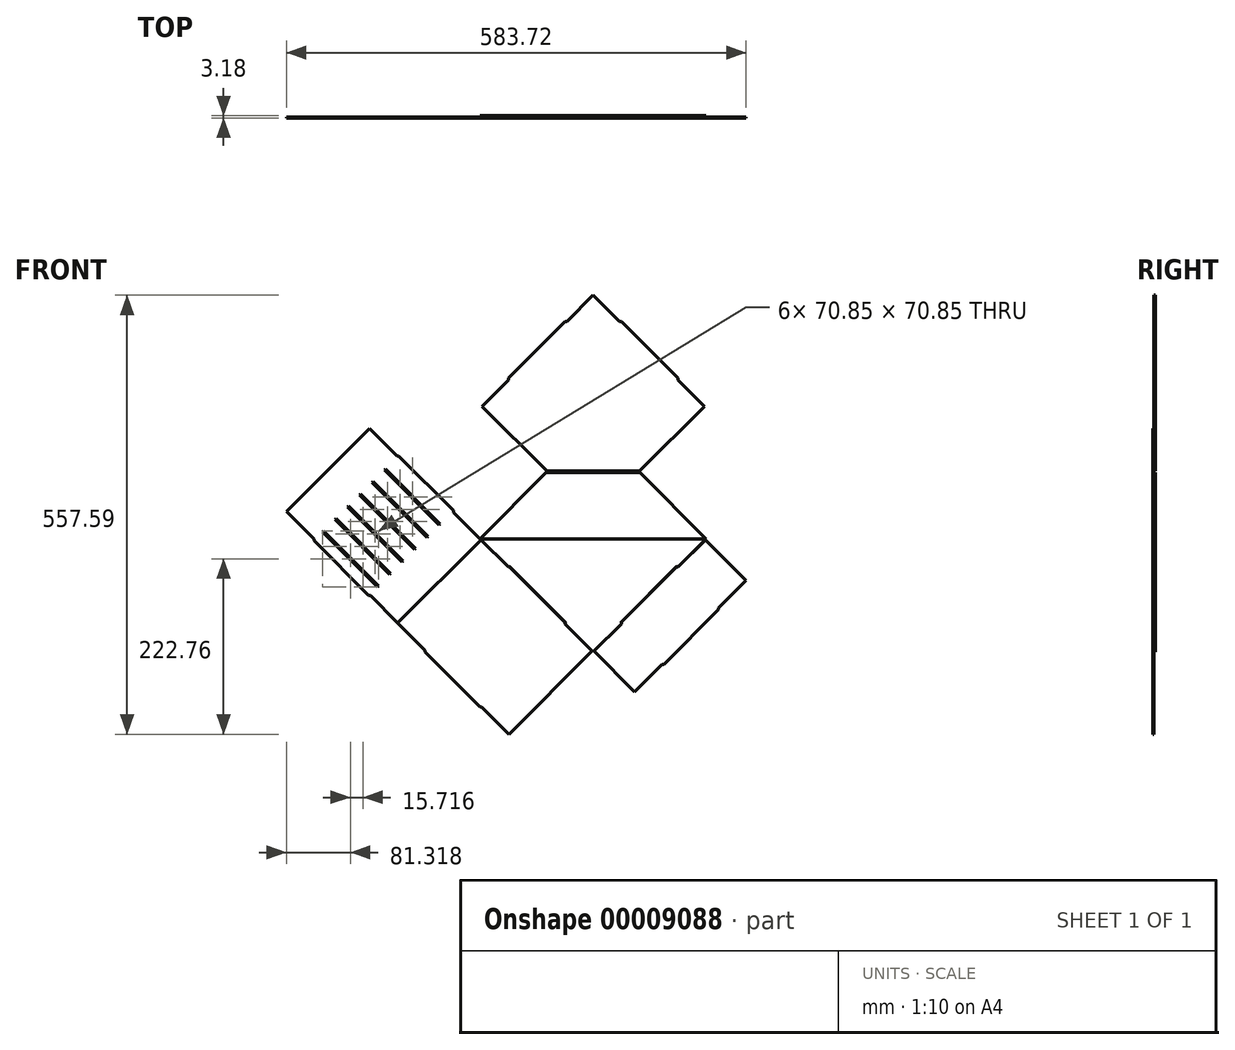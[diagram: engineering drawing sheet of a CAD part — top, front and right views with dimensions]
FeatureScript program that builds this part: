
annotation { "Feature Type Name" : "Feature", "Feature Type Description" : "" }
export const myFeature = defineFeature(function(context is Context, id is Id, definition is map)
    precondition{}
    {
        {
            var Q0;
            Q0=qCreatedBy(makeId("Front.planeOp"),FACE);
            var sketch = newSketch(context, id + "F0", { "sketchPlane" : qUnion([Q0])});
            skLineSegment(sketch, "E0", {"start": v(0, 0) * mm, "end": v(-143.68, 143.68) * mm});
            skLineSegment(sketch, "E1", {"start": v(-143.68, 143.68) * mm, "end": v(-59.52, 227.85) * mm});
            skLineSegment(sketch, "E2", {"start": v(59.52, 227.85) * mm, "end": v(143.68, 143.68) * mm});
            skLineSegment(sketch, "E3", {"start": v(143.68, 143.68) * mm, "end": v(0, 0) * mm});
            skLineSegment(sketch, "E4", {"start": v(-143.68, 143.68) * mm, "end": v(143.68, 143.68) * mm});
            skLineSegment(sketch, "E5", {"start": v(-35.92, 35.92) * mm, "end": v(-34.8, 37.04) * mm});
            skLineSegment(sketch, "E6", {"start": v(-34.8, 37.04) * mm, "end": v(-106.64, 108.89) * mm});
            skLineSegment(sketch, "E7", {"start": v(-106.64, 108.89) * mm, "end": v(-107.76, 107.76) * mm});
            skLineSegment(sketch, "E8", {"start": v(0, 0) * mm, "end": v(0, 287.37) * mm, "construction": true});
            skLineSegment(sketch, "E9.0.MirrorCS", {"start": v(35.92, 35.92) * mm, "end": v(34.8, 37.04) * mm});
            skLineSegment(sketch, "E9.1.MirrorCS", {"start": v(34.8, 37.04) * mm, "end": v(106.64, 108.89) * mm});
            skLineSegment(sketch, "E9.2.MirrorCS", {"start": v(106.64, 108.89) * mm, "end": v(107.76, 107.76) * mm});
            skLineSegment(sketch, "E10", {"start": v(-143.68, 143.68) * mm, "end": v(-249.2, 38.17) * mm});
            skLineSegment(sketch, "E11", {"start": v(-249.2, 38.17) * mm, "end": v(-105.52, -105.52) * mm});
            skLineSegment(sketch, "E12", {"start": v(-105.52, -105.52) * mm, "end": v(0, 0) * mm});
            skLineSegment(sketch, "E13", {"start": v(-196.44, 90.93) * mm, "end": v(-52.76, -52.76) * mm, "construction": true});
            skLineSegment(sketch, "E14.0.MirrorCS", {"start": v(-142.56, -70.72) * mm, "end": v(-214.4, 1.12) * mm});
            skLineSegment(sketch, "E15.0.MirrorCS", {"start": v(-214.4, 1.12) * mm, "end": v(-213.28, 2.25) * mm});
            skLineSegment(sketch, "E16.0.MirrorCS", {"start": v(-141.44, -69.6) * mm, "end": v(-142.56, -70.72) * mm});
            skLineSegment(sketch, "E17", {"start": v(143.68, 143.68) * mm, "end": v(195.32, 92.05) * mm});
            skLineSegment(sketch, "E18", {"start": v(195.32, 92.05) * mm, "end": v(51.64, -51.64) * mm});
            skLineSegment(sketch, "E19", {"start": v(51.64, -51.64) * mm, "end": v(0, 0) * mm});
            skLineSegment(sketch, "E20", {"start": v(169.5, 117.87) * mm, "end": v(25.82, -25.82) * mm, "construction": true});
            skLineSegment(sketch, "E21.0.MirrorCS", {"start": v(87.56, -15.72) * mm, "end": v(88.68, -16.84) * mm});
            skLineSegment(sketch, "E21.1.MirrorCS", {"start": v(87.56, -15.72) * mm, "end": v(88.68, -16.84) * mm});
            skLineSegment(sketch, "E21.2.MirrorCS", {"start": v(160.52, 55) * mm, "end": v(159.4, 56.13) * mm});
            skLineSegment(sketch, "E21.3.MirrorCS", {"start": v(160.52, 55) * mm, "end": v(159.4, 56.13) * mm});
            skLineSegment(sketch, "E21.4.MirrorCS", {"start": v(88.68, -16.84) * mm, "end": v(160.52, 55) * mm});
            skLineSegment(sketch, "E21.5.MirrorCS", {"start": v(88.68, -16.84) * mm, "end": v(160.52, 55) * mm});
            skLineSegment(sketch, "E22", {"start": v(-107.76, 107.76) * mm, "end": v(-105.52, 107.76) * mm});
            skLineSegment(sketch, "E23", {"start": v(-35.92, 35.92) * mm, "end": v(-35.92, 38.17) * mm});
            skLineSegment(sketch, "E24.0.MirrorCS", {"start": v(-213.28, 2.25) * mm, "end": v(-213.28, 0) * mm});
            skLineSegment(sketch, "E25.0.MirrorCS", {"start": v(-141.44, -69.6) * mm, "end": v(-143.68, -69.6) * mm});
            skLineSegment(sketch, "E26", {"start": v(35.92, 35.92) * mm, "end": v(35.92, 38.17) * mm});
            skLineSegment(sketch, "E27", {"start": v(107.76, 107.76) * mm, "end": v(105.52, 107.76) * mm});
            skLineSegment(sketch, "E28.0.MirrorCS", {"start": v(159.4, 56.13) * mm, "end": v(159.4, 53.88) * mm});
            skLineSegment(sketch, "E29.0.MirrorCS", {"start": v(87.56, -15.72) * mm, "end": v(89.8, -15.72) * mm});
            skLineSegment(sketch, "E30", {"start": v(-142.56, 142.56) * mm, "end": v(-248.08, 37.04) * mm});
            skLineSegment(sketch, "E31", {"start": v(-106.64, -104.4) * mm, "end": v(-1.12, 1.12) * mm});
            skLineSegment(sketch, "E32", {"start": v(52.76, -50.51) * mm, "end": v(1.12, 1.12) * mm});
            skLineSegment(sketch, "E33", {"start": v(142.56, 142.56) * mm, "end": v(194.2, 90.93) * mm});
            skLineSegment(sketch, "E34", {"start": v(-59.52, 227.85) * mm, "end": v(59.52, 227.85) * mm});
            skPoint(sketch, "E35.0.MirrorCS.end.orphan", {"position": v(34.8, 250.32) * mm});
            skPoint(sketch, "E35.0.MirrorCS.start.orphan", {"position": v(35.92, 251.45) * mm});
            skPoint(sketch, "E36.0.MirrorCS.end.orphan", {"position": v(-34.8, 250.32) * mm});
            skPoint(sketch, "E36.0.MirrorCS.start.orphan", {"position": v(-35.92, 251.45) * mm});
            skPoint(sketch, "E37.0.MirrorCS.end.orphan", {"position": v(107.76, 179.6) * mm});
            skPoint(sketch, "E37.0.MirrorCS.start.orphan", {"position": v(106.64, 178.48) * mm});
            skPoint(sketch, "E38.0.MirrorCS.end.orphan", {"position": v(-107.76, 179.6) * mm});
            skPoint(sketch, "E38.0.MirrorCS.start.orphan", {"position": v(-106.64, 178.48) * mm});
            skSolve(sketch);
        }
        {
            var Q0;
            {var subQ3=sQuery(id+"F0.wireOp",EDGE,"E4");Q0=makeQuery(id+"F0.imprint","IMPRINT",FACE,{"disambiguationData":[TD([[makeQuery(id+"F0.imprint","IMPRINT",EDGE,{"derivedFrom":subQ3}),-1.0]])]});}
            extrude(context, id + "F1", {"entities" : qUnion([Q0]), "depth" : 1.59 * mm});
        }
        {
            var Q0;
            {var subQ5=sQuery(id+"F0.wireOp",EDGE,"E4");Q0=makeQuery(id+"F0.imprint","IMPRINT",FACE,{"disambiguationData":[TD([[makeQuery(id+"F0.imprint","IMPRINT",EDGE,{"derivedFrom":subQ5}),1.0]])]});}
            var Q1;
            {var subQ3=sQuery(id+"F0.wireOp",EDGE,"E4");Q1=makeQuery(id+"F0.imprint","IMPRINT",FACE,{"disambiguationData":[TD([[makeQuery(id+"F0.imprint","IMPRINT",EDGE,{"derivedFrom":subQ3}),-1.0]])]});}
            var Q2;
            Q2=makeQuery(id+"F0.imprint","IMPRINT",FACE,{"disambiguationData":[TD([[makeQuery(id+"F0.imprint","IMPRINT",EDGE,{"derivedFrom":sQuery(id+"F0.wireOp",EDGE,"4ca332ba-a74b-4d34-af89-f9be247be29c.0.MirrorCS")}),1.0]])]});
            var Q3;
            {var subQ1=sQuery(id+"F0.wireOp",EDGE,"E36.0.MirrorCS");Q3=makeQuery(id+"F0.imprint","IMPRINT",FACE,{"disambiguationData":[TD([[makeQuery(id+"F0.imprint","IMPRINT",EDGE,{"derivedFrom":subQ1}),-1.0]])]});}
            extrude(context, id + "F2", {"entities" : qUnion([Q0, Q1, Q2, Q3]), "oppositeDirection" : true, "depth" : 1.59 * mm});
        }
        {
            var Q0;
            {var subQ2=sQuery(id+"F0.wireOp",EDGE,"E24.0.MirrorCS");Q0=makeQuery(id+"F0.imprint","IMPRINT",FACE,{"disambiguationData":[TD([[makeQuery(id+"F0.imprint","IMPRINT",EDGE,{"derivedFrom":subQ2}),1.0]])]});}
            var Q1;
            {var subQ1=sQuery(id+"F0.wireOp",EDGE,"E22");Q1=makeQuery(id+"F0.imprint","IMPRINT",FACE,{"disambiguationData":[TD([[makeQuery(id+"F0.imprint","IMPRINT",EDGE,{"derivedFrom":subQ1}),-1.0]])]});}
            var Q2;
            {var subQ1=sQuery(id+"F0.wireOp",EDGE,"E30");Q2=makeQuery(id+"F0.imprint","IMPRINT",FACE,{"disambiguationData":[TD([[makeQuery(id+"F0.imprint","IMPRINT",EDGE,{"derivedFrom":subQ1}),1.0]])]});}
            extrude(context, id + "F3", {"entities" : qUnion([Q0, Q1, Q2]), "depth" : 1.59 * mm});
        }
        {
            var Q0;
            {var subQ1=sQuery(id+"F0.wireOp",EDGE,"E26");Q0=makeQuery(id+"F0.imprint","IMPRINT",FACE,{"disambiguationData":[TD([[makeQuery(id+"F0.imprint","IMPRINT",EDGE,{"derivedFrom":subQ1}),-1.0]])]});}
            var Q1;
            {var subQ1=sQuery(id+"F0.wireOp",EDGE,"E28.0.MirrorCS");Q1=makeQuery(id+"F0.imprint","IMPRINT",FACE,{"disambiguationData":[TD([[makeQuery(id+"F0.imprint","IMPRINT",EDGE,{"derivedFrom":subQ1}),-1.0]])]});}
            var Q2;
            {var subQ1=sQuery(id+"F0.wireOp",EDGE,"E32");Q2=makeQuery(id+"F0.imprint","IMPRINT",FACE,{"disambiguationData":[TD([[makeQuery(id+"F0.imprint","IMPRINT",EDGE,{"derivedFrom":subQ1}),-1.0]])]});}
            extrude(context, id + "F4", {"entities" : qUnion([Q0, Q1, Q2]), "depth" : 1.59 * mm});
        }
        {
            var Q0;
            Q0=makeQuery(id+"F3.opExtrude","SWEPT_BODY",BODY,{"disambiguationData":[OSD([sQuery(id+"F0.wireOp",EDGE,"E0"),sQuery(id+"F0.wireOp",EDGE,"E6"),sQuery(id+"F0.wireOp",EDGE,"E11"),sQuery(id+"F0.wireOp",EDGE,"E14.0.MirrorCS"),sQuery(id+"F0.wireOp",EDGE,"E22"),sQuery(id+"F0.wireOp",EDGE,"E23"),sQuery(id+"F0.wireOp",EDGE,"E24.0.MirrorCS"),sQuery(id+"F0.wireOp",EDGE,"E25.0.MirrorCS"),sQuery(id+"F0.wireOp",EDGE,"E30"),sQuery(id+"F0.wireOp",EDGE,"E31")])]});
            var Q1;
            Q1=makeQuery(id+"F3.opExtrude","SWEPT_FACE",FACE,{"disambiguationData":[OSD([sQuery(id+"F0.wireOp",EDGE,"E30")])]});
            mirror(context, id + "F5", {"entities" : qUnion([Q0]), "mirrorPlane" : qUnion([Q1])});
        }
        {
            var Q0;
            Q0=makeQuery(id+"F5.opPattern","COPY",FACE,{"derivedFrom":makeQuery(id+"F3.opExtrude","CAP_FACE",FACE,{"disambiguationData":[OSD([sQuery(id+"F0.wireOp",EDGE,"E0"),sQuery(id+"F0.wireOp",EDGE,"E6"),sQuery(id+"F0.wireOp",EDGE,"E11"),sQuery(id+"F0.wireOp",EDGE,"E14.0.MirrorCS"),sQuery(id+"F0.wireOp",EDGE,"E22"),sQuery(id+"F0.wireOp",EDGE,"E23"),sQuery(id+"F0.wireOp",EDGE,"E24.0.MirrorCS"),sQuery(id+"F0.wireOp",EDGE,"E25.0.MirrorCS"),sQuery(id+"F0.wireOp",EDGE,"E30"),sQuery(id+"F0.wireOp",EDGE,"E31")])],"isStart":false}),"instanceName":"1"});
            var sketch = newSketch(context, id + "F6", { "sketchPlane" : qUnion([Q0])});
            skLineSegment(sketch, "E39.0.0", {"start": v(-354.72, 143.68) * mm, "end": v(-354.72, 141.44) * mm});
            skLineSegment(sketch, "E39.0.1", {"start": v(-354.72, 141.44) * mm, "end": v(-285.12, 71.84) * mm});
            skLineSegment(sketch, "E39.0.2", {"start": v(-285.12, 71.84) * mm, "end": v(-282.88, 71.84) * mm});
            skLineSegment(sketch, "E39.0.3", {"start": v(-282.88, 71.84) * mm, "end": v(-248.08, 37.04) * mm});
            skLineSegment(sketch, "E39.0.4", {"start": v(-248.08, 37.04) * mm, "end": v(-142.56, 142.56) * mm});
            skLineSegment(sketch, "E39.0.5", {"start": v(-142.56, 142.56) * mm, "end": v(-177.36, 177.36) * mm});
            skLineSegment(sketch, "E39.0.6", {"start": v(-177.36, 177.36) * mm, "end": v(-177.36, 179.6) * mm});
            skLineSegment(sketch, "E39.0.7", {"start": v(-177.36, 179.6) * mm, "end": v(-246.96, 249.2) * mm});
            skLineSegment(sketch, "E39.0.8", {"start": v(-246.96, 249.2) * mm, "end": v(-249.2, 249.2) * mm});
            skLineSegment(sketch, "E39.0.9", {"start": v(-249.2, 249.2) * mm, "end": v(-284, 284) * mm});
            skLineSegment(sketch, "E39.0.10", {"start": v(-284, 284) * mm, "end": v(-389.52, 178.48) * mm});
            skLineSegment(sketch, "E39.0.11", {"start": v(-389.52, 178.48) * mm, "end": v(-354.72, 143.68) * mm});
            skLineSegment(sketch, "E40", {"start": v(-194.2, 162.77) * mm, "end": v(-263.8, 232.36) * mm});
            skLineSegment(sketch, "E41", {"start": v(-263.8, 232.36) * mm, "end": v(-265.05, 231.1) * mm});
            skLineSegment(sketch, "E42", {"start": v(-265.05, 231.1) * mm, "end": v(-195.46, 161.5) * mm});
            skLineSegment(sketch, "E43", {"start": v(-195.46, 161.5) * mm, "end": v(-194.2, 162.77) * mm});
            skLineSegment(sketch, "E44.1.0.0", {"start": v(-279.51, 216.65) * mm, "end": v(-280.77, 215.4) * mm});
            skLineSegment(sketch, "E44.1.0.1", {"start": v(-280.77, 215.4) * mm, "end": v(-211.17, 145.8) * mm});
            skLineSegment(sketch, "E44.1.0.2", {"start": v(-209.91, 147.05) * mm, "end": v(-279.51, 216.65) * mm});
            skLineSegment(sketch, "E44.1.0.3", {"start": v(-211.17, 145.8) * mm, "end": v(-209.91, 147.05) * mm});
            skLineSegment(sketch, "E44.2.0.0", {"start": v(-295.23, 200.93) * mm, "end": v(-296.48, 199.68) * mm});
            skLineSegment(sketch, "E44.2.0.1", {"start": v(-296.48, 199.68) * mm, "end": v(-226.89, 130.08) * mm});
            skLineSegment(sketch, "E44.2.0.2", {"start": v(-225.63, 131.34) * mm, "end": v(-295.23, 200.93) * mm});
            skLineSegment(sketch, "E44.2.0.3", {"start": v(-226.89, 130.08) * mm, "end": v(-225.63, 131.34) * mm});
            skLineSegment(sketch, "E44.3.0.0", {"start": v(-310.94, 185.22) * mm, "end": v(-312.2, 183.96) * mm});
            skLineSegment(sketch, "E44.3.0.1", {"start": v(-312.2, 183.96) * mm, "end": v(-242.6, 114.36) * mm});
            skLineSegment(sketch, "E44.3.0.2", {"start": v(-241.34, 115.62) * mm, "end": v(-310.94, 185.22) * mm});
            skLineSegment(sketch, "E44.3.0.3", {"start": v(-242.6, 114.36) * mm, "end": v(-241.34, 115.62) * mm});
            skLineSegment(sketch, "E44.4.0.0", {"start": v(-326.66, 169.5) * mm, "end": v(-327.91, 168.25) * mm});
            skLineSegment(sketch, "E44.4.0.1", {"start": v(-327.91, 168.25) * mm, "end": v(-258.32, 98.65) * mm});
            skLineSegment(sketch, "E44.4.0.2", {"start": v(-257.06, 99.9) * mm, "end": v(-326.66, 169.5) * mm});
            skLineSegment(sketch, "E44.4.0.3", {"start": v(-258.32, 98.65) * mm, "end": v(-257.06, 99.9) * mm});
            skLineSegment(sketch, "E44.5.0.0", {"start": v(-342.37, 153.79) * mm, "end": v(-343.63, 152.53) * mm});
            skLineSegment(sketch, "E44.5.0.1", {"start": v(-343.63, 152.53) * mm, "end": v(-274.03, 82.93) * mm});
            skLineSegment(sketch, "E44.5.0.2", {"start": v(-272.78, 84.19) * mm, "end": v(-342.37, 153.79) * mm});
            skLineSegment(sketch, "E44.5.0.3", {"start": v(-274.03, 82.93) * mm, "end": v(-272.78, 84.19) * mm});
            skLineSegment(sketch, "E44.direction1", {"start": v(-263.8, 232.36) * mm, "end": v(-279.51, 216.65) * mm, "construction": true});
            skSolve(sketch);
        }
        {
            var Q0;
            Q0=makeQuery(id+"F6.imprint","IMPRINT",FACE,{"disambiguationData":[TD([[makeQuery(id+"F6.imprint","IMPRINT",EDGE,{"derivedFrom":sQuery(id+"F6.wireOp",EDGE,"E40")}),1.0]])]});
            var Q1;
            Q1=makeQuery(id+"F6.imprint","IMPRINT",FACE,{"disambiguationData":[TD([[makeQuery(id+"F6.imprint","IMPRINT",EDGE,{"derivedFrom":sQuery(id+"F6.wireOp",EDGE,"E44.1.0.0")}),1.0]])]});
            var Q2;
            Q2=makeQuery(id+"F6.imprint","IMPRINT",FACE,{"disambiguationData":[TD([[makeQuery(id+"F6.imprint","IMPRINT",EDGE,{"derivedFrom":sQuery(id+"F6.wireOp",EDGE,"E44.2.0.0")}),1.0]])]});
            var Q3;
            Q3=makeQuery(id+"F6.imprint","IMPRINT",FACE,{"disambiguationData":[TD([[makeQuery(id+"F6.imprint","IMPRINT",EDGE,{"derivedFrom":sQuery(id+"F6.wireOp",EDGE,"E44.3.0.0")}),1.0]])]});
            var Q4;
            Q4=makeQuery(id+"F6.imprint","IMPRINT",FACE,{"disambiguationData":[TD([[makeQuery(id+"F6.imprint","IMPRINT",EDGE,{"derivedFrom":sQuery(id+"F6.wireOp",EDGE,"E44.4.0.0")}),1.0]])]});
            var Q5;
            Q5=makeQuery(id+"F6.imprint","IMPRINT",FACE,{"disambiguationData":[TD([[makeQuery(id+"F6.imprint","IMPRINT",EDGE,{"derivedFrom":sQuery(id+"F6.wireOp",EDGE,"E44.5.0.0")}),1.0]])]});
            var Q6;
            Q6=makeQuery(id+"F6.imprint","IMPRINT",FACE,{"disambiguationData":[TD([[makeQuery(id+"F6.imprint","IMPRINT",EDGE,{"derivedFrom":sQuery(id+"F6.wireOp",EDGE,"E44.6.0.0")}),1.0]])]});
            var Q7;
            Q7=makeQuery(id+"F6.imprint","IMPRINT",FACE,{"disambiguationData":[TD([[makeQuery(id+"F6.imprint","IMPRINT",EDGE,{"derivedFrom":sQuery(id+"F6.wireOp",EDGE,"E44.7.0.0")}),1.0]])]});
            extrude(context, id + "F7", {"entities" : qUnion([Q0, Q1, Q2, Q3, Q4, Q5, Q6, Q7]), "operationType" : NewBodyOperationType.REMOVE, "oppositeDirection" : true, "depth" : 25.4 * mm});
        }
        {
            var Q0;
            Q0=makeQuery(id+"F2.opExtrude","SWEPT_BODY",BODY,{"disambiguationData":[OSD([sQuery(id+"F0.wireOp",EDGE,"E0"),sQuery(id+"F0.wireOp",EDGE,"E1"),sQuery(id+"F0.wireOp",EDGE,"E2"),sQuery(id+"F0.wireOp",EDGE,"E3"),sQuery(id+"F0.wireOp",EDGE,"E5"),sQuery(id+"F0.wireOp",EDGE,"E6"),sQuery(id+"F0.wireOp",EDGE,"E7"),sQuery(id+"F0.wireOp",EDGE,"E9.1.MirrorCS"),sQuery(id+"F0.wireOp",EDGE,"E9.2.MirrorCS"),sQuery(id+"F0.wireOp",EDGE,"E9.0.MirrorCS"),sQuery(id+"F0.wireOp",EDGE,"E34")])]});
            var Q1;
            Q1=makeQuery(id+"F2.opExtrude","SWEPT_FACE",FACE,{"disambiguationData":[OSD([sQuery(id+"F0.wireOp",EDGE,"E34")])]});
            mirror(context, id + "F8", {"entities" : qUnion([Q0]), "mirrorPlane" : qUnion([Q1])});
        }
        {
            var Q0;
            Q0=makeQuery(id+"F8.opPattern","COPY",FACE,{"derivedFrom":makeQuery(id+"F2.opExtrude","CAP_FACE",FACE,{"disambiguationData":[OSD([sQuery(id+"F0.wireOp",EDGE,"E0"),sQuery(id+"F0.wireOp",EDGE,"E1"),sQuery(id+"F0.wireOp",EDGE,"E2"),sQuery(id+"F0.wireOp",EDGE,"E3"),sQuery(id+"F0.wireOp",EDGE,"E5"),sQuery(id+"F0.wireOp",EDGE,"E6"),sQuery(id+"F0.wireOp",EDGE,"E7"),sQuery(id+"F0.wireOp",EDGE,"E9.1.MirrorCS"),sQuery(id+"F0.wireOp",EDGE,"E9.2.MirrorCS"),sQuery(id+"F0.wireOp",EDGE,"E9.0.MirrorCS"),sQuery(id+"F0.wireOp",EDGE,"E34")])],"isStart":true}),"instanceName":"1"});
            var sketch = newSketch(context, id + "F9", { "sketchPlane" : qUnion([Q0])});
            skLineSegment(sketch, "E45.0", {"start": v(33.4, 419.78) * mm, "end": v(0, 453.2) * mm});
            skLineSegment(sketch, "E45.1", {"start": v(33.4, 419.78) * mm, "end": v(32.28, 418.66) * mm});
            skLineSegment(sketch, "E45.2", {"start": v(32.28, 418.66) * mm, "end": v(106.64, 344.3) * mm});
            skLineSegment(sketch, "E45.3", {"start": v(106.64, 344.3) * mm, "end": v(107.76, 345.43) * mm});
            skLineSegment(sketch, "E45.4", {"start": v(141.17, 312.02) * mm, "end": v(107.76, 345.43) * mm});
            skLineSegment(sketch, "E45.5", {"start": v(0, 453.2) * mm, "end": v(-33.4, 419.78) * mm});
            skLineSegment(sketch, "E45.6", {"start": v(58.78, 229.63) * mm, "end": v(141.17, 312.02) * mm});
            skLineSegment(sketch, "E45.7", {"start": v(-58.78, 229.63) * mm, "end": v(58.78, 229.63) * mm});
            skLineSegment(sketch, "E45.8", {"start": v(-141.17, 312.02) * mm, "end": v(-58.78, 229.63) * mm});
            skLineSegment(sketch, "E45.9", {"start": v(-107.76, 345.43) * mm, "end": v(-141.17, 312.02) * mm});
            skLineSegment(sketch, "E45.10", {"start": v(-106.64, 344.3) * mm, "end": v(-107.76, 345.43) * mm});
            skLineSegment(sketch, "E45.11", {"start": v(-32.28, 418.66) * mm, "end": v(-106.64, 344.3) * mm});
            skLineSegment(sketch, "E45.12", {"start": v(-33.4, 419.78) * mm, "end": v(-32.28, 418.66) * mm});
            skLineSegment(sketch, "E46", {"start": v(-33.4, 419.78) * mm, "end": v(-107.76, 345.43) * mm});
            skLineSegment(sketch, "E47", {"start": v(107.76, 345.43) * mm, "end": v(33.4, 419.78) * mm});
            skLineSegment(sketch, "E48", {"start": v(-33.4, 419.78) * mm, "end": v(-35.92, 419.78) * mm});
            skLineSegment(sketch, "E49", {"start": v(-107.76, 345.43) * mm, "end": v(-107.76, 347.94) * mm});
            skLineSegment(sketch, "E50", {"start": v(107.76, 345.43) * mm, "end": v(107.76, 347.94) * mm});
            skLineSegment(sketch, "E51", {"start": v(33.4, 419.78) * mm, "end": v(35.92, 419.78) * mm});
            skLineSegment(sketch, "E52", {"start": v(-35.92, 419.78) * mm, "end": v(-107.76, 347.94) * mm});
            skLineSegment(sketch, "E53", {"start": v(35.92, 419.78) * mm, "end": v(107.76, 347.94) * mm});
            skSolve(sketch);
        }
        {
            var Q0;
            Q0=makeQuery(id+"F9.imprint","IMPRINT",FACE,{"disambiguationData":[TD([[makeQuery(id+"F9.imprint","IMPRINT",EDGE,{"derivedFrom":sQuery(id+"F9.wireOp",EDGE,"E45.0")}),-1.0]])]});
            var Q1;
            Q1=makeQuery(id+"F9.imprint","IMPRINT",FACE,{"disambiguationData":[TD([[makeQuery(id+"F9.imprint","IMPRINT",EDGE,{"derivedFrom":sQuery(id+"F9.wireOp",EDGE,"E45.4")}),-1.0]])]});
            extrude(context, id + "F10", {"entities" : qUnion([Q0, Q1]), "operationType" : NewBodyOperationType.REMOVE, "oppositeDirection" : true, "depth" : 25.4 * mm});
        }
        {
            var Q0;
            {var subQ3=makeQuery(id+"F8.opPattern","COPY",EDGE,{"derivedFrom":makeQuery(id+"F2.opExtrude","CAP_EDGE",EDGE,{"disambiguationData":[OSD([sQuery(id+"F0.wireOp",EDGE,"E6")])],"isStart":true}),"instanceName":"1"});Q0=makeQuery(id+"F9.imprint","IMPRINT",FACE,{"disambiguationData":[TD([[makeQuery(id+"F9.imprint","IMPRINT",EDGE,{"derivedFrom":subQ3}),-1.0]])]});}
            var Q1;
            {var subQ3=makeQuery(id+"F8.opPattern","COPY",EDGE,{"derivedFrom":makeQuery(id+"F2.opExtrude","CAP_EDGE",EDGE,{"disambiguationData":[OSD([sQuery(id+"F0.wireOp",EDGE,"E9.1.MirrorCS")])],"isStart":true}),"instanceName":"1"});Q1=makeQuery(id+"F9.imprint","IMPRINT",FACE,{"disambiguationData":[TD([[makeQuery(id+"F9.imprint","IMPRINT",EDGE,{"derivedFrom":subQ3}),1.0]])]});}
            var Q2;
            Q2=makeQuery(id+"F9.imprint","IMPRINT",FACE,{"disambiguationData":[TD([[makeQuery(id+"F9.imprint","IMPRINT",EDGE,{"derivedFrom":sQuery(id+"F9.wireOp",EDGE,"E46")}),-1.0]])]});
            var Q3;
            Q3=makeQuery(id+"F9.imprint","IMPRINT",FACE,{"disambiguationData":[TD([[makeQuery(id+"F9.imprint","IMPRINT",EDGE,{"derivedFrom":sQuery(id+"F9.wireOp",EDGE,"E47")}),-1.0]])]});
            extrude(context, id + "F11", {"entities" : qUnion([Q0, Q1, Q2, Q3]), "operationType" : NewBodyOperationType.ADD, "oppositeDirection" : true, "depth" : 1.59 * mm});
        }
    });
